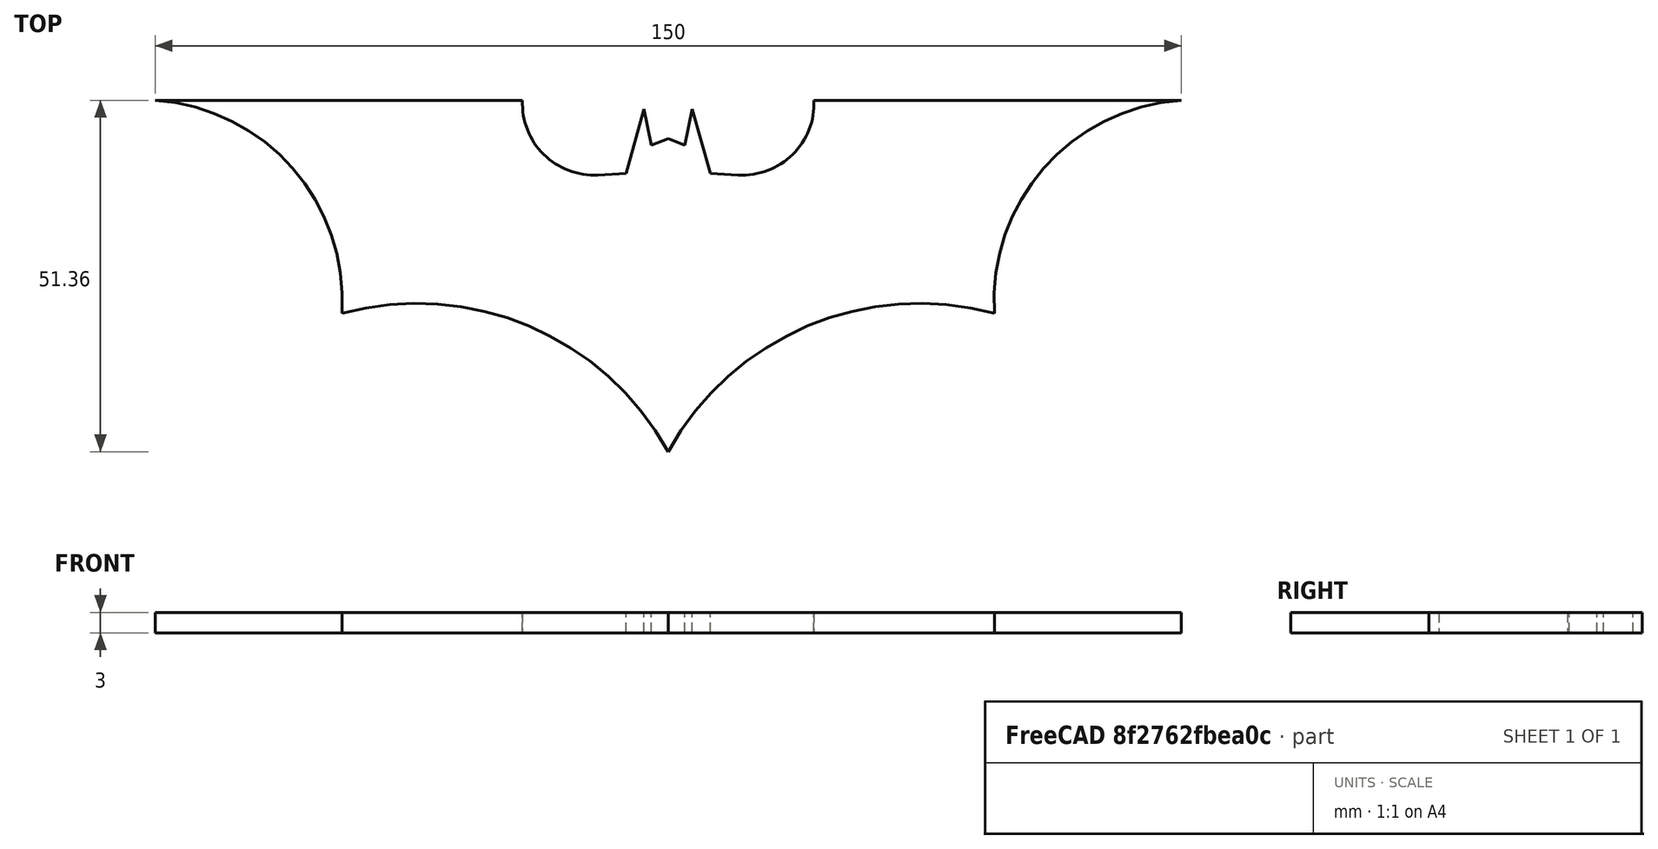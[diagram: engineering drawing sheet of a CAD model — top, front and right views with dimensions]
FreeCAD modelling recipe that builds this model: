
FCSTD DOCUMENT  (FreeCAD 0.17R13523 (Git))
Label: batarang
License: All rights reserved
LicenseURL: http://en.wikipedia.org/wiki/All_rights_reserved
objects: Sketcher::SketchObject×1, PartDesign::Pad×1, PartDesign::Mirrored×1, PartDesign::Body×1
note: 5 computed .brp shape members not serialized (recipe doc carries the construction recipe); baked Part::Feature solids carry a one-line shape summary decoded from their .brp

FEATURE [Sketcher::SketchObject] Sketch
  MapMode = 5
  Support = -> [XY_Plane001]
  sketch-geometry (10):
    g0: LineSegment StartX=0 StartY=0 StartZ=0 EndX=0 EndY=14.5025 EndZ=0
    g1: LineSegment StartX=0 StartY=14.5025 StartZ=0 EndX=2.44464 EndY=13.5418 EndZ=0
    g2: LineSegment StartX=2.44464 StartY=13.5418 StartZ=0 EndX=3.52541 EndY=18.8256 EndZ=0
    g3: LineSegment StartX=3.52541 StartY=18.8256 StartZ=0 EndX=6.16731 EndY=9.45904 EndZ=0
    g4: LineSegment StartX=6.16731 StartY=9.45904 StartZ=0 EndX=10.2503 EndY=9.2183 EndZ=0
    g5: ArcOfCircle CenterX=10.8649 CenterY=19.6433 CenterZ=0 NormalX=0 NormalY=0 NormalZ=1 AngleXU=0 Radius=10.4431 StartAngle=4.6535 EndAngle=6.3293
    g6: LineSegment StartX=21.297 StartY=20.1248 StartZ=0 EndX=75 EndY=20.1248 EndZ=0
    g7: ArcOfCircle CenterX=76.9474 CenterY=-9.11961 CenterZ=0 NormalX=0 NormalY=0 NormalZ=1 AngleXU=0 Radius=29.3092 StartAngle=1.63729 EndAngle=3.20691
    g8: ArcOfCircle CenterX=36.6975 CenterY=-51.4672 CenterZ=0 NormalX=0 NormalY=0 NormalZ=1 AngleXU=0 Radius=41.9049 StartAngle=1.3051 EndAngle=2.63775
    g9: LineSegment StartX=0 StartY=-31.2358 StartZ=0 EndX=0 EndY=0 EndZ=0
  constraints (18):
    c: Coincident(g-1,g0)
    c: Vertical(g0)
    c: Coincident(g0,g1)
    c: Coincident(g1,g2)
    c: Coincident(g2,g3)
    c: Coincident(g3,g4)
    c: Tangent(g4,g5) = -1.5708
    c: Coincident(g5,g6)
    c: Coincident(g7,g6)
    c: Horizontal(g6)
    c: DistanceX(g6) = 75
    c: DistanceY(g6) = 20.1248
    c: DistanceX(g7) = 47.7008
    c: DistanceY(g7) = -11.0328
    c: Coincident(g8,g7)
    c: PointOnObject(g8,g-2)
    c: Coincident(g9,g8)
    c: Coincident(g9,g-1)
FEATURE [PartDesign::Pad] Pad
  Length = 3
  Length2 = 100
  Profile = -> Sketch
  Type = 0
FEATURE [PartDesign::Mirrored] Mirrored
  BaseFeature = -> Pad
  MirrorPlane = -> Sketch [V_Axis]
  Originals = -> [Pad]
  Refine = true
FEATURE [PartDesign::Body] Body001  label="Body"
  Group = -> [Sketch,Pad,Mirrored]
  Origin = -> Origin001
  Tip = -> Mirrored
